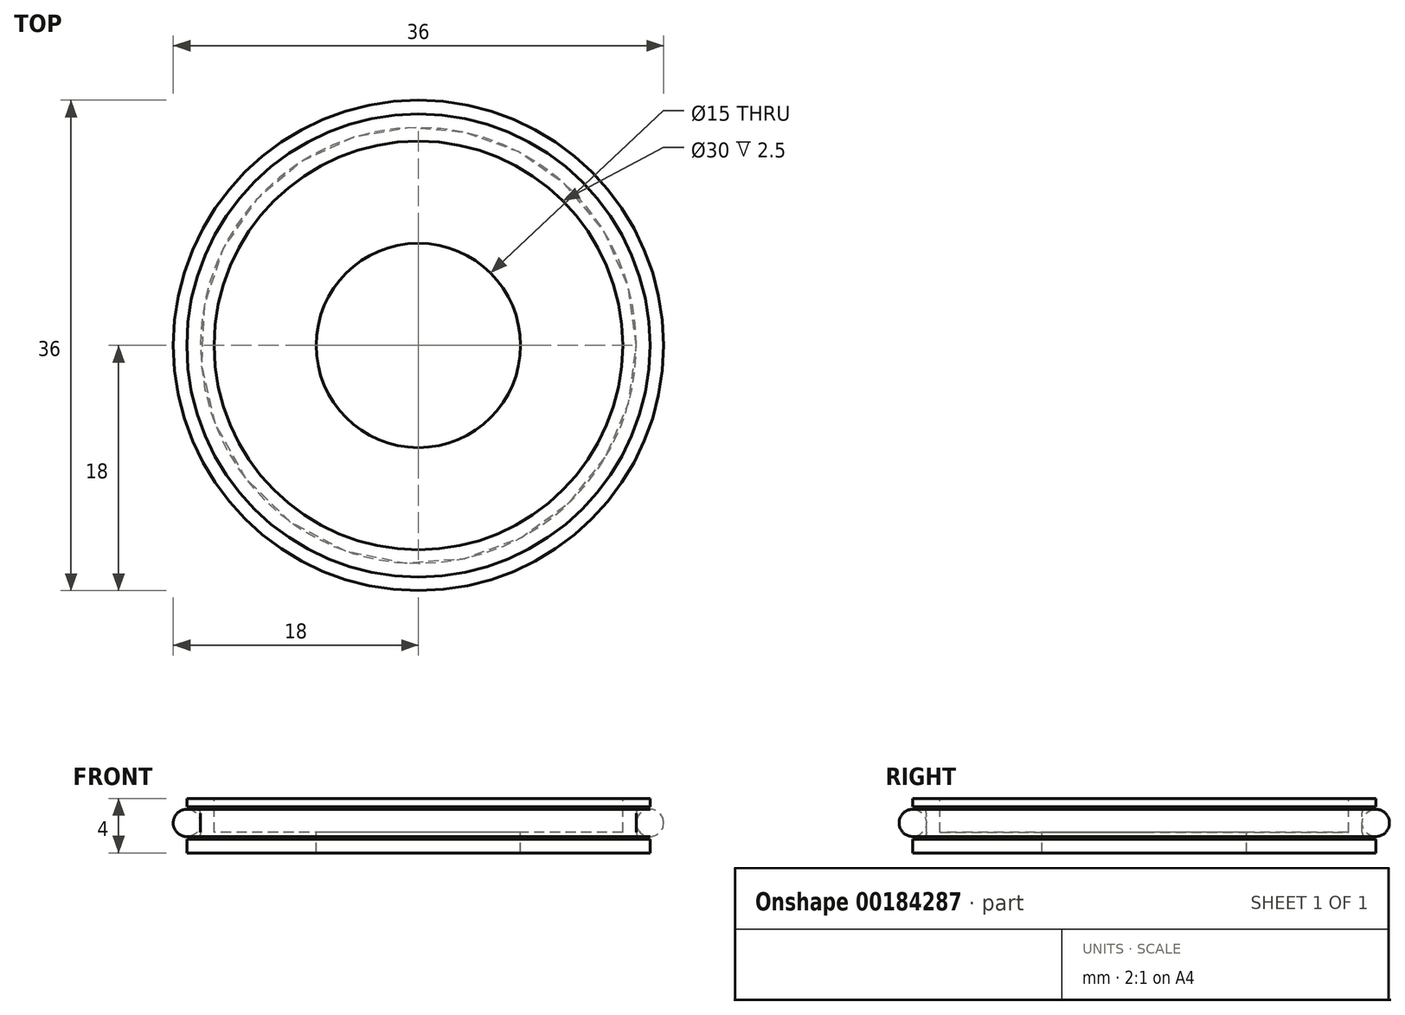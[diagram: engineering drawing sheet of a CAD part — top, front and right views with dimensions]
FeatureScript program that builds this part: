
annotation { "Feature Type Name" : "Feature", "Feature Type Description" : "" }
export const myFeature = defineFeature(function(context is Context, id is Id, definition is map)
    precondition{}
    {
        {
            var Q0;
            Q0=qCreatedBy(makeId("Front.planeOp"),FACE);
            var sketch = newSketch(context, id + "F0", { "sketchPlane" : qUnion([Q0])});
            skLineSegment(sketch, "E0", {"start": v(0, 12.26) * mm, "end": v(0, -12.12) * mm, "construction": true});
            skLineSegment(sketch, "E1", {"start": v(12.08, 0) * mm, "end": v(-12.22, 0) * mm, "construction": true});
            skLineSegment(sketch, "E2.bottom", {"start": v(-17, 4) * mm, "end": v(-15, 4) * mm});
            skLineSegment(sketch, "E2.top", {"start": v(-17, 0) * mm, "end": v(-15, 0) * mm});
            skLineSegment(sketch, "E2.left", {"start": v(-17, 4) * mm, "end": v(-17, 3.4) * mm});
            skLineSegment(sketch, "E2.right", {"start": v(-15, 4) * mm, "end": v(-15, 1.5) * mm});
            skLineSegment(sketch, "E3.bottom", {"start": v(-15, 1.5) * mm, "end": v(-7.5, 1.5) * mm});
            skLineSegment(sketch, "E3.top", {"start": v(-17, 0) * mm, "end": v(-7.5, 0) * mm});
            skLineSegment(sketch, "E3.left", {"start": v(-17, 1) * mm, "end": v(-17, 0) * mm});
            skLineSegment(sketch, "E3.right", {"start": v(-7.5, 1.5) * mm, "end": v(-7.5, 0) * mm});
            skLineSegment(sketch, "E4.bottom", {"start": v(-17, 3.4) * mm, "end": v(-16.5, 3.4) * mm});
            skLineSegment(sketch, "E4.top", {"start": v(-17, 1) * mm, "end": v(-16.5, 1) * mm});
            skLineSegment(sketch, "E4.right", {"start": v(-16, 2.9) * mm, "end": v(-16, 1.5) * mm});
            skPoint(sketch, "E5.visualSharp", {"position": v(-16, 3.4) * mm});
            skArc(sketch, "E5.filletArc", {"start": v(-16, 2.9) * mm, "mid": v(-16.15, 3.25) * mm, "end": v(-16.5, 3.4) * mm});
            skPoint(sketch, "E6.visualSharp", {"position": v(-16, 1) * mm});
            skArc(sketch, "E6.filletArc", {"start": v(-16.5, 1) * mm, "mid": v(-16.15, 1.15) * mm, "end": v(-16, 1.5) * mm});
            skCircle(sketch, "E7", {"center": v(-17, 2.2) * mm, "radius": 1 * mm});
            skPoint(sketch, "E8", {"position": v(-16, 2.2) * mm});
            skLineSegment(sketch, "E9", {"start": v(-16, 2.2) * mm, "end": v(-43.5, 2.2) * mm, "construction": true});
            skSolve(sketch);
        }
        {
            var Q0;
            Q0=makeQuery(id+"F0.imprint","IMPRINT",FACE,{"disambiguationData":[TD([[makeQuery(id+"F0.imprint","IMPRINT",EDGE,{"derivedFrom":sQuery(id+"F0.wireOp",EDGE,"E2.bottom")}),-1.0]])]});
            var Q1;
            Q1=makeQuery(id+"F0.imprint","IMPRINT",FACE,{"disambiguationData":[TD([[makeQuery(id+"F0.imprint","IMPRINT",EDGE,{"derivedFrom":sQuery(id+"F0.wireOp",EDGE,"E7")}),1.0]])]});
            var Q2;
            Q2=sQuery(id+"F0.wireOp",EDGE,"E0");
            revolve(context, id + "F1", {"entities" : qUnion([Q0, Q1]), "axis" : qUnion([Q2]), "revolveType" : RevolveType.FULL});
        }
    });
